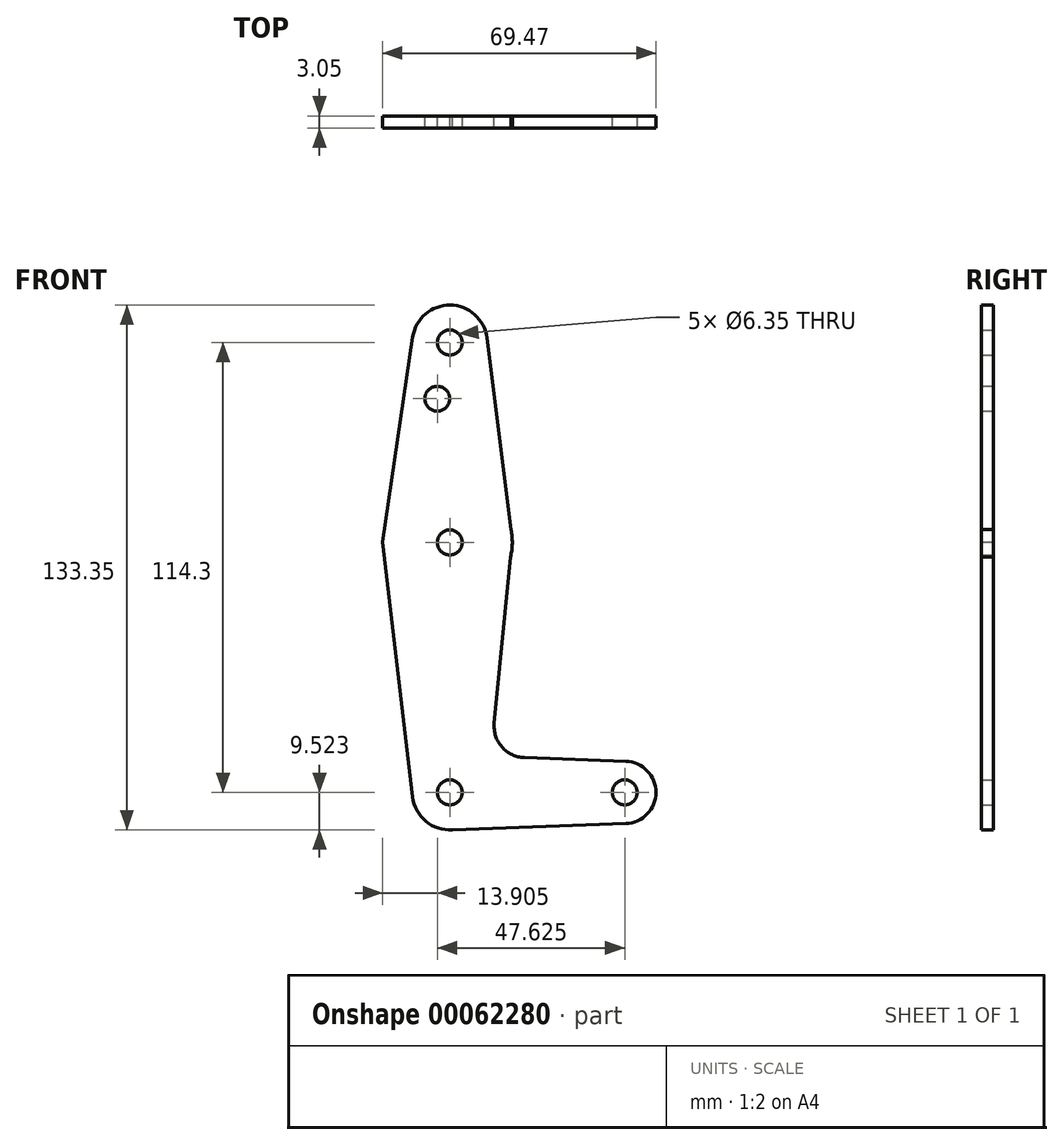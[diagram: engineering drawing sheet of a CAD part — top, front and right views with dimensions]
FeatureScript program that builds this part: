
annotation { "Feature Type Name" : "Feature", "Feature Type Description" : "" }
export const myFeature = defineFeature(function(context is Context, id is Id, definition is map)
    precondition{}
    {
        {
            var Q0;
            Q0=qCreatedBy(makeId("Front.planeOp"),FACE);
            var sketch = newSketch(context, id + "F0", { "sketchPlane" : qUnion([Q0])});
            skLineSegment(sketch, "E0", {"start": v(0, 67.25) * mm, "end": v(0, 16.45) * mm, "construction": true});
            skLineSegment(sketch, "E1", {"start": v(0, 16.45) * mm, "end": v(0, -47.05) * mm, "construction": true});
            skLineSegment(sketch, "E2", {"start": v(0, -47.05) * mm, "end": v(44.45, -47.05) * mm, "construction": true});
            skCircle(sketch, "E3", {"center": v(0, 67.25) * mm, "radius": 9.53 * mm});
            skCircle(sketch, "E4", {"center": v(0, -47.05) * mm, "radius": 9.53 * mm});
            skCircle(sketch, "E5", {"center": v(44.45, -47.05) * mm, "radius": 7.94 * mm});
            skCircle(sketch, "E6", {"center": v(0, 16.45) * mm, "radius": 15.88 * mm});
            skLineSegment(sketch, "E7", {"start": v(15.86, 17.1) * mm, "end": v(9.45, 68.43) * mm});
            skLineSegment(sketch, "E8", {"start": v(-9.42, 68.64) * mm, "end": v(-17.08, 16.6) * mm});
            skLineSegment(sketch, "E9", {"start": v(15.86, 17.1) * mm, "end": v(11.3, -29.48) * mm});
            skLineSegment(sketch, "E10", {"start": v(-17.08, 16.6) * mm, "end": v(-9.46, -48.16) * mm});
            skLineSegment(sketch, "E11", {"start": v(0, -56.57) * mm, "end": v(44.73, -54.98) * mm});
            skLineSegment(sketch, "E12", {"start": v(44.73, -39.11) * mm, "end": v(18.92, -38.2) * mm});
            skCircle(sketch, "E13", {"center": v(0, 67.25) * mm, "radius": 3.18 * mm});
            skCircle(sketch, "E14", {"center": v(-3.17, 52.98) * mm, "radius": 3.18 * mm});
            skCircle(sketch, "E15", {"center": v(0, 16.45) * mm, "radius": 3.18 * mm});
            skCircle(sketch, "E16", {"center": v(0, -47.05) * mm, "radius": 3.18 * mm});
            skCircle(sketch, "E17", {"center": v(44.45, -47.05) * mm, "radius": 3.18 * mm});
            skArc(sketch, "E18.filletArc", {"start": v(11.3, -29.48) * mm, "mid": v(13.22, -35.49) * mm, "end": v(18.92, -38.2) * mm});
            skSolve(sketch);
        }
        {
            var Q0;
            Q0 = qSketchRegion(id + "F0", true);
            extrude(context, id + "F1", {"entities" : qUnion([Q0]), "depth" : 3.05 * mm});
        }
    });
